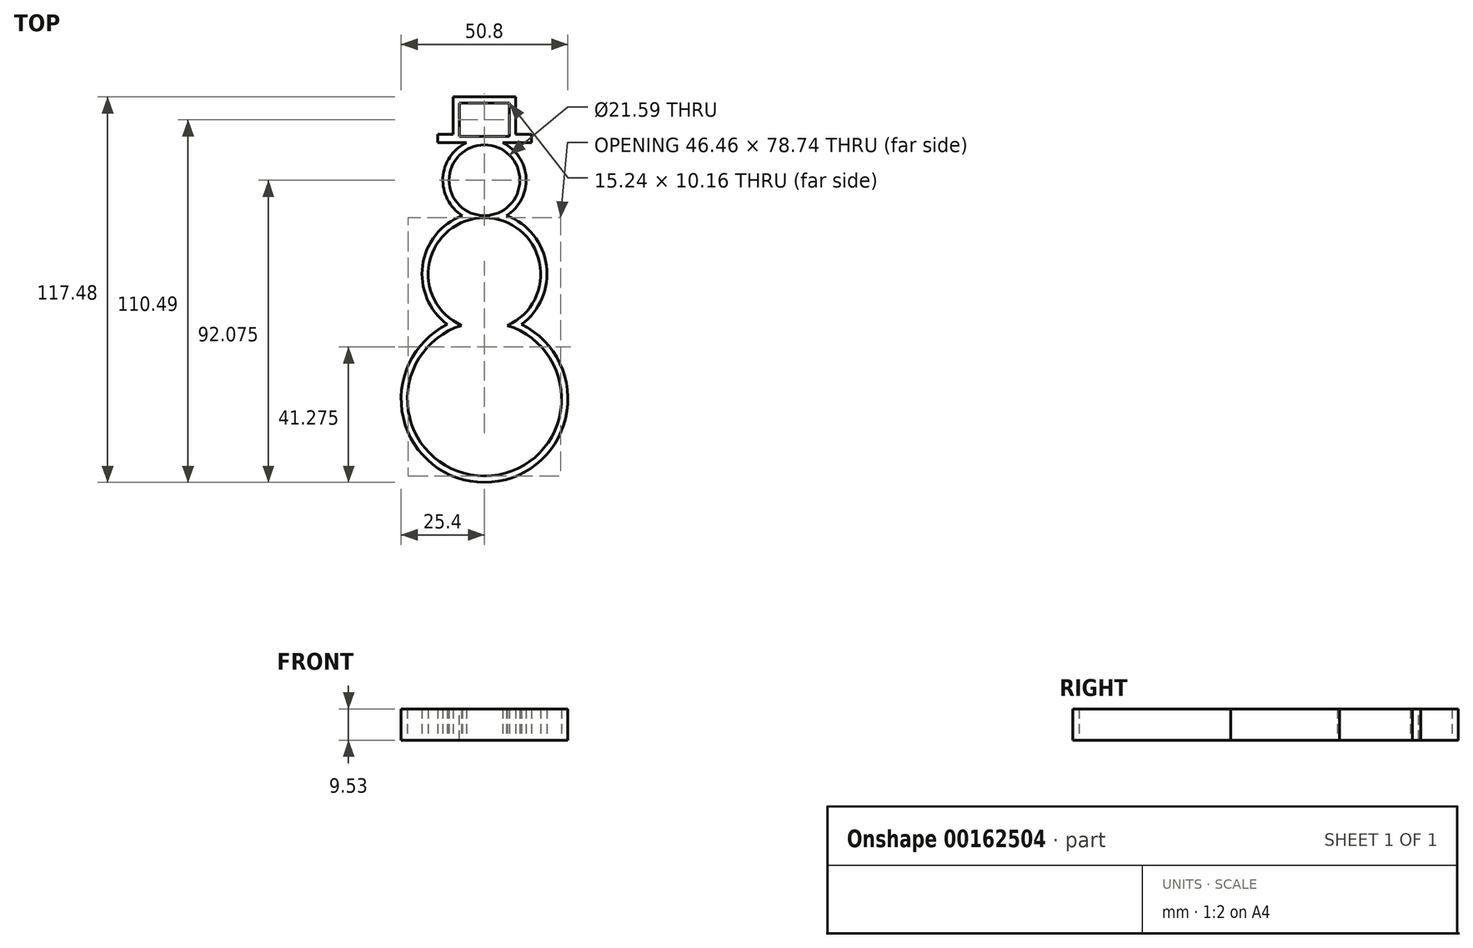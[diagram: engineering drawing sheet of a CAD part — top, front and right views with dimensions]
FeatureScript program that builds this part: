
annotation { "Feature Type Name" : "Feature", "Feature Type Description" : "" }
export const myFeature = defineFeature(function(context is Context, id is Id, definition is map)
    precondition{}
    {
        {
            var Q0;
            Q0=qCreatedBy(makeId("Top.planeOp"),FACE);
            var sketch = newSketch(context, id + "F0", { "sketchPlane" : qUnion([Q0])});
            skArc(sketch, "E0", {"start": v(-6.75, 17.82) * mm, "mid": v(-18.87, 2.58) * mm, "end": v(-11.29, -15.35) * mm});
            skArc(sketch, "E1", {"start": v(6.75, 17.82) * mm, "mid": v(0, 41.28) * mm, "end": v(-6.75, 17.82) * mm});
            skArc(sketch, "E2", {"start": v(-11.29, -15.35) * mm, "mid": v(0, -63.5) * mm, "end": v(11.29, -15.35) * mm});
            skArc(sketch, "E3.trimOffspring", {"start": v(11.29, -15.35) * mm, "mid": v(18.87, 2.58) * mm, "end": v(6.75, 17.82) * mm});
            skLineSegment(sketch, "E4.bottom", {"start": v(0, 41.28) * mm, "end": v(9.53, 41.28) * mm});
            skLineSegment(sketch, "E4.top", {"start": v(-9.53, 53.98) * mm, "end": v(9.53, 53.98) * mm});
            skLineSegment(sketch, "E4.left", {"start": v(-9.53, 42.55) * mm, "end": v(-9.53, 53.98) * mm});
            skLineSegment(sketch, "E4.right", {"start": v(9.52, 41.28) * mm, "end": v(9.52, 53.98) * mm});
            skPoint(sketch, "E4.middle", {"position": v(0, 47.62) * mm});
            skPoint(sketch, "E5.cornerSnap0", {"position": v(0, 41.28) * mm});
            skLineSegment(sketch, "E6.bottom", {"start": v(-14.29, 40) * mm, "end": v(-5.54, 40) * mm});
            skLineSegment(sketch, "E6.top", {"start": v(-14.29, 42.55) * mm, "end": v(-9.53, 42.55) * mm});
            skLineSegment(sketch, "E6.left", {"start": v(-14.29, 40) * mm, "end": v(-14.29, 42.55) * mm});
            skLineSegment(sketch, "E6.right", {"start": v(14.29, 40) * mm, "end": v(14.29, 42.55) * mm});
            skLineSegment(sketch, "E7.trimOffspring", {"start": v(9.52, 42.55) * mm, "end": v(14.29, 42.55) * mm});
            skPoint(sketch, "E8.orphan", {"position": v(-9.53, 41.27) * mm});
            skLineSegment(sketch, "E9.trimOffspring", {"start": v(5.54, 40) * mm, "end": v(14.29, 40) * mm});
            skSolve(sketch);
        }
        {
            var Q0;
            Q0 = qSketchRegion(id + "F0", true);
            extrude(context, id + "F1", {"entities" : qUnion([Q0]), "depth" : 9.52 * mm});
        }
        {
            var Q0;
            Q0=makeQuery(id+"F1.opExtrude","CAP_FACE",FACE,{"disambiguationData":[OSD([sQuery(id+"F0.wireOp",EDGE,"E0"),sQuery(id+"F0.wireOp",EDGE,"E1"),sQuery(id+"F0.wireOp",EDGE,"E2"),sQuery(id+"F0.wireOp",EDGE,"E3.trimOffspring"),sQuery(id+"F0.wireOp",EDGE,"E4.top"),sQuery(id+"F0.wireOp",EDGE,"E4.left"),sQuery(id+"F0.wireOp",EDGE,"E4.right"),sQuery(id+"F0.wireOp",EDGE,"E6.bottom"),sQuery(id+"F0.wireOp",EDGE,"E6.top"),sQuery(id+"F0.wireOp",EDGE,"E6.left"),sQuery(id+"F0.wireOp",EDGE,"E6.right"),sQuery(id+"F0.wireOp",EDGE,"E7.trimOffspring"),sQuery(id+"F0.wireOp",EDGE,"E9.trimOffspring")])],"isStart":false});
            var Q1;
            Q1=makeQuery(id+"F1.opExtrude","CAP_FACE",FACE,{"disambiguationData":[OSD([sQuery(id+"F0.wireOp",EDGE,"E0"),sQuery(id+"F0.wireOp",EDGE,"E1"),sQuery(id+"F0.wireOp",EDGE,"E2"),sQuery(id+"F0.wireOp",EDGE,"E3.trimOffspring"),sQuery(id+"F0.wireOp",EDGE,"E4.top"),sQuery(id+"F0.wireOp",EDGE,"E4.left"),sQuery(id+"F0.wireOp",EDGE,"E4.right"),sQuery(id+"F0.wireOp",EDGE,"E6.bottom"),sQuery(id+"F0.wireOp",EDGE,"E6.top"),sQuery(id+"F0.wireOp",EDGE,"E6.left"),sQuery(id+"F0.wireOp",EDGE,"E6.right"),sQuery(id+"F0.wireOp",EDGE,"E7.trimOffspring"),sQuery(id+"F0.wireOp",EDGE,"E9.trimOffspring")])],"isStart":true});
            shell(context, id + "F2", {"entities" : qUnion([Q0, Q1]), "thickness" : 1.9 * mm});
        }
    });
